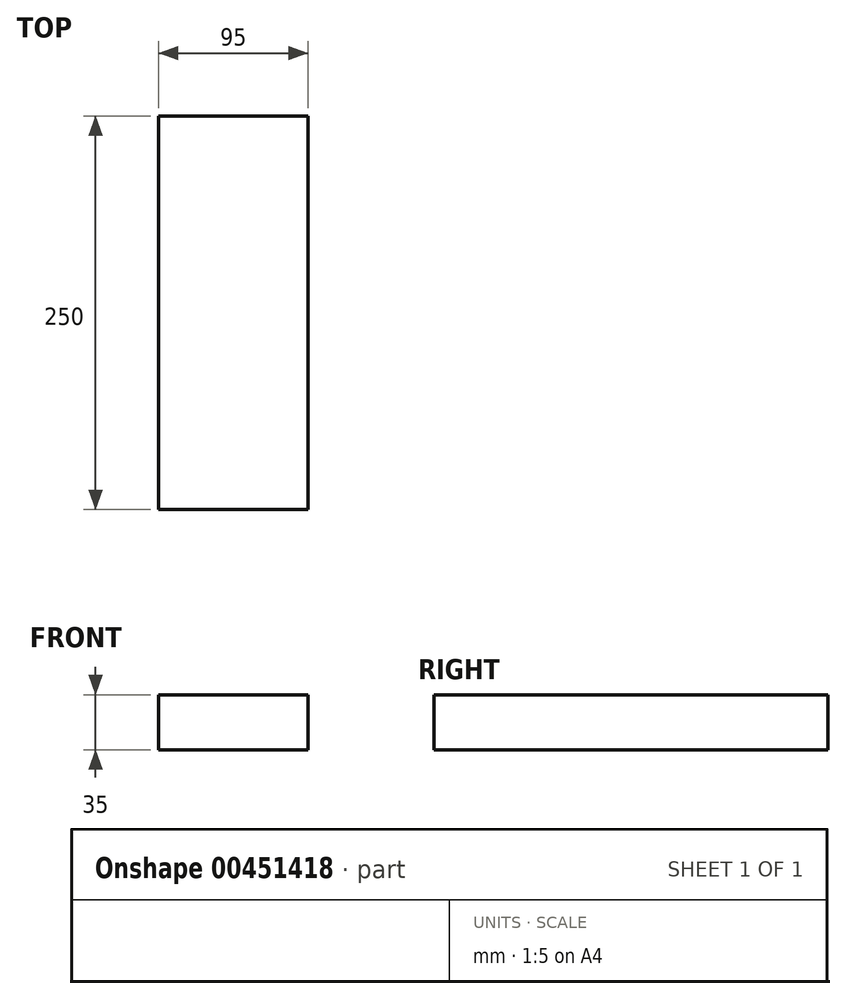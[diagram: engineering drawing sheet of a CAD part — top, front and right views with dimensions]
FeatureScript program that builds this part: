
annotation { "Feature Type Name" : "Feature", "Feature Type Description" : "" }
export const myFeature = defineFeature(function(context is Context, id is Id, definition is map)
    precondition{}
    {
        {
            var Q0;
            Q0=qCreatedBy(makeId("Front.planeOp"),FACE);
            var sketch = newSketch(context, id + "F0", { "sketchPlane" : qUnion([Q0])});
            skLineSegment(sketch, "E0.bottom", {"start": v(47.5, 17.5) * mm, "end": v(-47.5, 17.5) * mm});
            skLineSegment(sketch, "E0.top", {"start": v(47.5, -17.5) * mm, "end": v(-47.5, -17.5) * mm});
            skLineSegment(sketch, "E0.left", {"start": v(47.5, 17.5) * mm, "end": v(47.5, -17.5) * mm});
            skLineSegment(sketch, "E0.right", {"start": v(-47.5, 17.5) * mm, "end": v(-47.5, -17.5) * mm});
            skPoint(sketch, "E0.middle", {"position": v(0, 0) * mm});
            skLineSegment(sketch, "E1.bottom", {"start": v(149.17, 67.5) * mm, "end": v(69.17, 67.5) * mm});
            skLineSegment(sketch, "E1.top", {"start": v(149.17, 112.5) * mm, "end": v(69.17, 112.5) * mm});
            skLineSegment(sketch, "E1.left", {"start": v(149.17, 67.5) * mm, "end": v(149.17, 112.5) * mm});
            skLineSegment(sketch, "E1.right", {"start": v(69.17, 67.5) * mm, "end": v(69.17, 112.5) * mm});
            skPoint(sketch, "E1.middle", {"position": v(109.17, 90) * mm});
            skLineSegment(sketch, "E2", {"start": v(47.5, 17.5) * mm, "end": v(47.5, 60.15) * mm});
            skArc(sketch, "E3", {"start": v(68.03, 80.15) * mm, "mid": v(53.55, 74.48) * mm, "end": v(47.5, 60.15) * mm});
            skLineSegment(sketch, "E4", {"start": v(68.03, 80.15) * mm, "end": v(101.6, 80.15) * mm});
            skLineSegment(sketch, "E5.0", {"start": v(68.3, 105.15) * mm, "end": v(101.6, 105.15) * mm});
            skArc(sketch, "E5.1", {"start": v(68.3, 105.15) * mm, "mid": v(35.96, 92.25) * mm, "end": v(22.5, 60.15) * mm});
            skLineSegment(sketch, "E5.2", {"start": v(22.5, 17.5) * mm, "end": v(22.5, 60.15) * mm});
            skLineSegment(sketch, "E6", {"start": v(101.6, 67.5) * mm, "end": v(101.6, 112.5) * mm});
            skFitSpline(sketch, "E7", {"points": [v(-47.5, 17.5) * mm, v(68.3, 105.15) * mm], "startDerivative": vector(-0.2, 115.54) * mm, "endDerivative": vector(240.24, 5.2) * mm});
            skSolve(sketch);
        }
        {
            var Q0;
            Q0=makeQuery(id+"F0.imprint","IMPRINT",FACE,{"disambiguationData":[TD([[makeQuery(id+"F0.imprint","IMPRINT",EDGE,{"derivedFrom":sQuery(id+"F0.wireOp",EDGE,"E0.top")}),-1.0]])]});
            extrude(context, id + "F1", {"entities" : qUnion([Q0]), "depth" : 250 * mm});
        }
    });
